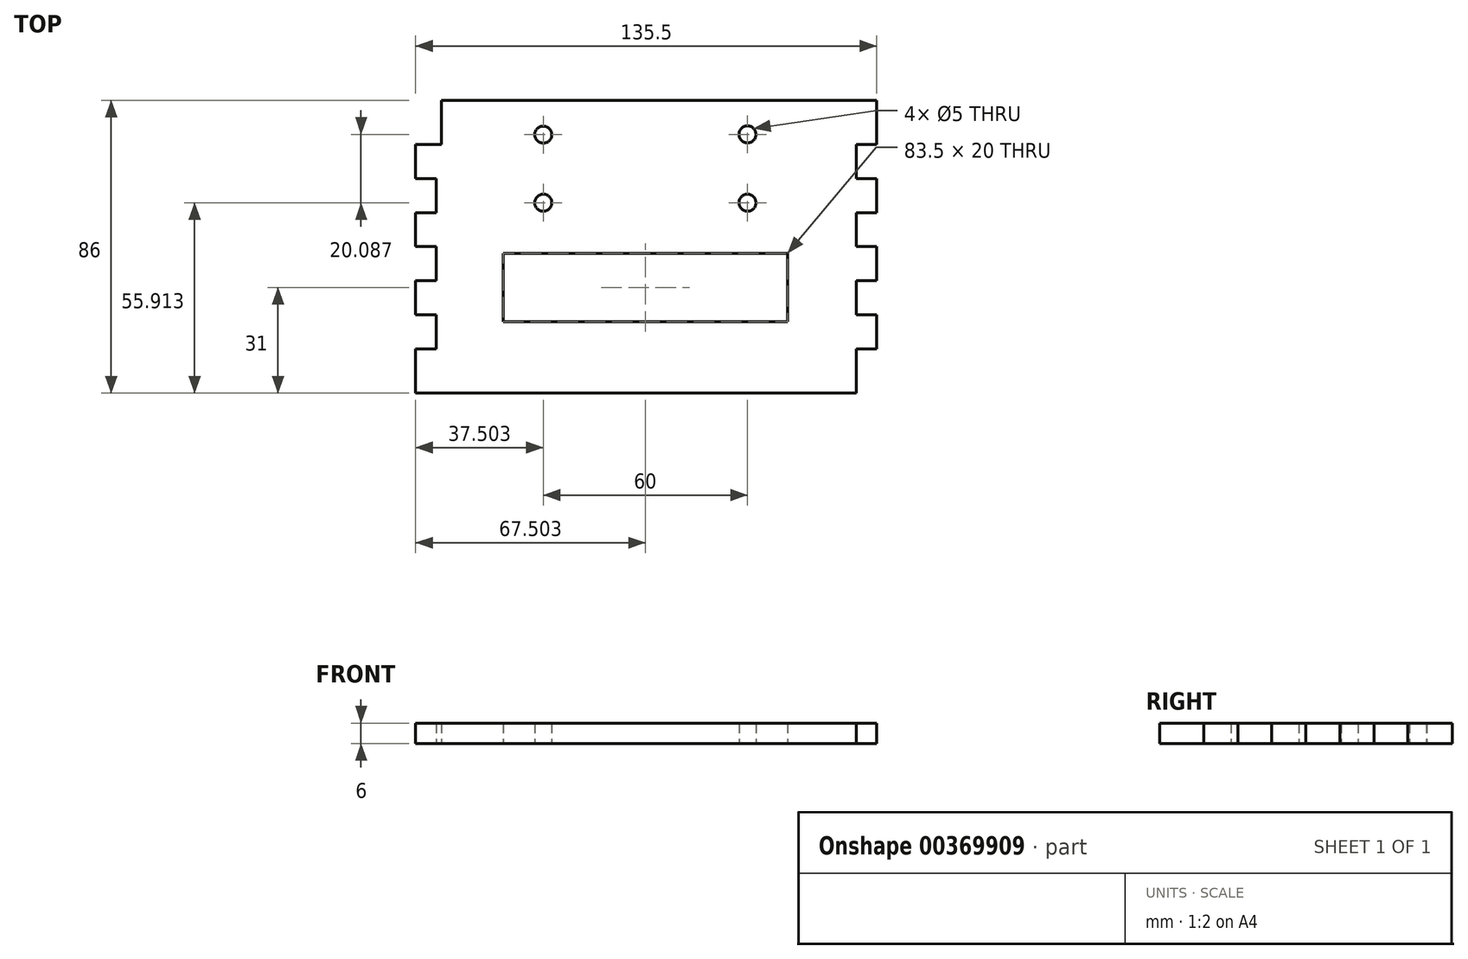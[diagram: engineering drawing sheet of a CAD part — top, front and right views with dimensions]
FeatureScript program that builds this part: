
annotation { "Feature Type Name" : "Feature", "Feature Type Description" : "" }
export const myFeature = defineFeature(function(context is Context, id is Id, definition is map)
    precondition{}
    {
        {
            var Q0;
            Q0=qCreatedBy(makeId("Top.planeOp"),FACE);
            var sketch = newSketch(context, id + "F0", { "sketchPlane" : qUnion([Q0])});
            skLineSegment(sketch, "E0", {"start": v(-46.65, -33) * mm, "end": v(82.85, -33) * mm});
            skLineSegment(sketch, "E1", {"start": v(82.85, -33) * mm, "end": v(82.85, -20) * mm});
            skLineSegment(sketch, "E2", {"start": v(82.85, -20) * mm, "end": v(88.85, -20) * mm});
            skLineSegment(sketch, "E3", {"start": v(88.85, -20) * mm, "end": v(88.85, -10) * mm});
            skLineSegment(sketch, "E4", {"start": v(88.85, -10) * mm, "end": v(82.85, -10) * mm});
            skLineSegment(sketch, "E5", {"start": v(82.85, -10) * mm, "end": v(82.85, 0) * mm});
            skLineSegment(sketch, "E6", {"start": v(82.85, 0) * mm, "end": v(88.85, 0) * mm});
            skLineSegment(sketch, "E7", {"start": v(88.85, 0) * mm, "end": v(88.85, 10) * mm});
            skLineSegment(sketch, "E8", {"start": v(88.85, 10) * mm, "end": v(82.85, 10) * mm});
            skLineSegment(sketch, "E9", {"start": v(82.85, 10) * mm, "end": v(82.85, 20) * mm});
            skLineSegment(sketch, "E10", {"start": v(82.85, 20) * mm, "end": v(88.85, 20) * mm});
            skLineSegment(sketch, "E11", {"start": v(-40.65, 20) * mm, "end": v(-46.65, 20) * mm});
            skLineSegment(sketch, "E12", {"start": v(-46.65, 20) * mm, "end": v(-46.65, 10) * mm});
            skLineSegment(sketch, "E13", {"start": v(-46.65, 10) * mm, "end": v(-40.65, 10) * mm});
            skLineSegment(sketch, "E14", {"start": v(-40.65, 10) * mm, "end": v(-40.65, 0) * mm});
            skLineSegment(sketch, "E15", {"start": v(-40.65, 0) * mm, "end": v(-46.65, 0) * mm});
            skLineSegment(sketch, "E16", {"start": v(-46.65, 0) * mm, "end": v(-46.65, -10) * mm});
            skLineSegment(sketch, "E17", {"start": v(-46.65, -10) * mm, "end": v(-40.65, -10) * mm});
            skLineSegment(sketch, "E18", {"start": v(-40.65, -10) * mm, "end": v(-40.65, -20) * mm});
            skLineSegment(sketch, "E19", {"start": v(-40.65, -20) * mm, "end": v(-46.65, -20) * mm});
            skLineSegment(sketch, "E20", {"start": v(-46.65, -20) * mm, "end": v(-46.65, -33) * mm});
            skLineSegment(sketch, "E21", {"start": v(-40.65, 20) * mm, "end": v(-40.65, 30) * mm});
            skLineSegment(sketch, "E22", {"start": v(-40.65, 30) * mm, "end": v(-46.65, 30) * mm});
            skLineSegment(sketch, "E23", {"start": v(-46.65, 30) * mm, "end": v(-46.65, 40) * mm});
            skLineSegment(sketch, "E24", {"start": v(-46.65, 40) * mm, "end": v(-39.15, 40) * mm});
            skLineSegment(sketch, "E25", {"start": v(-39.15, 40) * mm, "end": v(-39.15, 53) * mm});
            skLineSegment(sketch, "E26", {"start": v(-39.15, 53) * mm, "end": v(88.85, 53) * mm});
            skLineSegment(sketch, "E27", {"start": v(88.85, 53) * mm, "end": v(88.85, 40) * mm});
            skLineSegment(sketch, "E28", {"start": v(88.85, 40) * mm, "end": v(82.85, 40) * mm});
            skLineSegment(sketch, "E29", {"start": v(82.85, 40) * mm, "end": v(82.85, 30) * mm});
            skLineSegment(sketch, "E30", {"start": v(82.85, 30) * mm, "end": v(88.85, 30) * mm});
            skLineSegment(sketch, "E31", {"start": v(88.85, 30) * mm, "end": v(88.85, 20) * mm});
            skLineSegment(sketch, "E32", {"start": v(88.85, -10) * mm, "end": v(88.85, -12) * mm});
            skCircle(sketch, "E33", {"center": v(-9.15, 42.91) * mm, "radius": 2.5 * mm});
            skCircle(sketch, "E34", {"center": v(50.85, 43) * mm, "radius": 2.5 * mm});
            skCircle(sketch, "E35", {"center": v(-9.15, 22.91) * mm, "radius": 2.5 * mm});
            skCircle(sketch, "E36", {"center": v(50.85, 22.91) * mm, "radius": 2.5 * mm});
            skLineSegment(sketch, "E37", {"start": v(62.6, 0) * mm, "end": v(62.6, -12) * mm});
            skLineSegment(sketch, "E38", {"start": v(62.6, -12) * mm, "end": v(62.6, 8) * mm});
            skPoint(sketch, "E39.endSnap0", {"position": v(20.85, 0) * mm});
            skLineSegment(sketch, "E40", {"start": v(-20.9, 0) * mm, "end": v(-20.9, -12) * mm});
            skLineSegment(sketch, "E41", {"start": v(-20.9, -12) * mm, "end": v(-20.9, 8) * mm});
            skLineSegment(sketch, "E42", {"start": v(-20.9, 8) * mm, "end": v(62.6, 8) * mm});
            skLineSegment(sketch, "E43", {"start": v(-20.9, -12) * mm, "end": v(62.6, -12) * mm});
            skSolve(sketch);
        }
        {
            var Q0;
            Q0=makeQuery(id+"F0.imprint","IMPRINT",FACE,{"disambiguationData":[TD([[makeQuery(id+"F0.imprint","IMPRINT",EDGE,{"derivedFrom":sQuery(id+"F0.wireOp",EDGE,"E0")}),1.0]])]});
            extrude(context, id + "F1", {"entities" : qUnion([Q0]), "depth" : 6 * mm});
        }
    });
